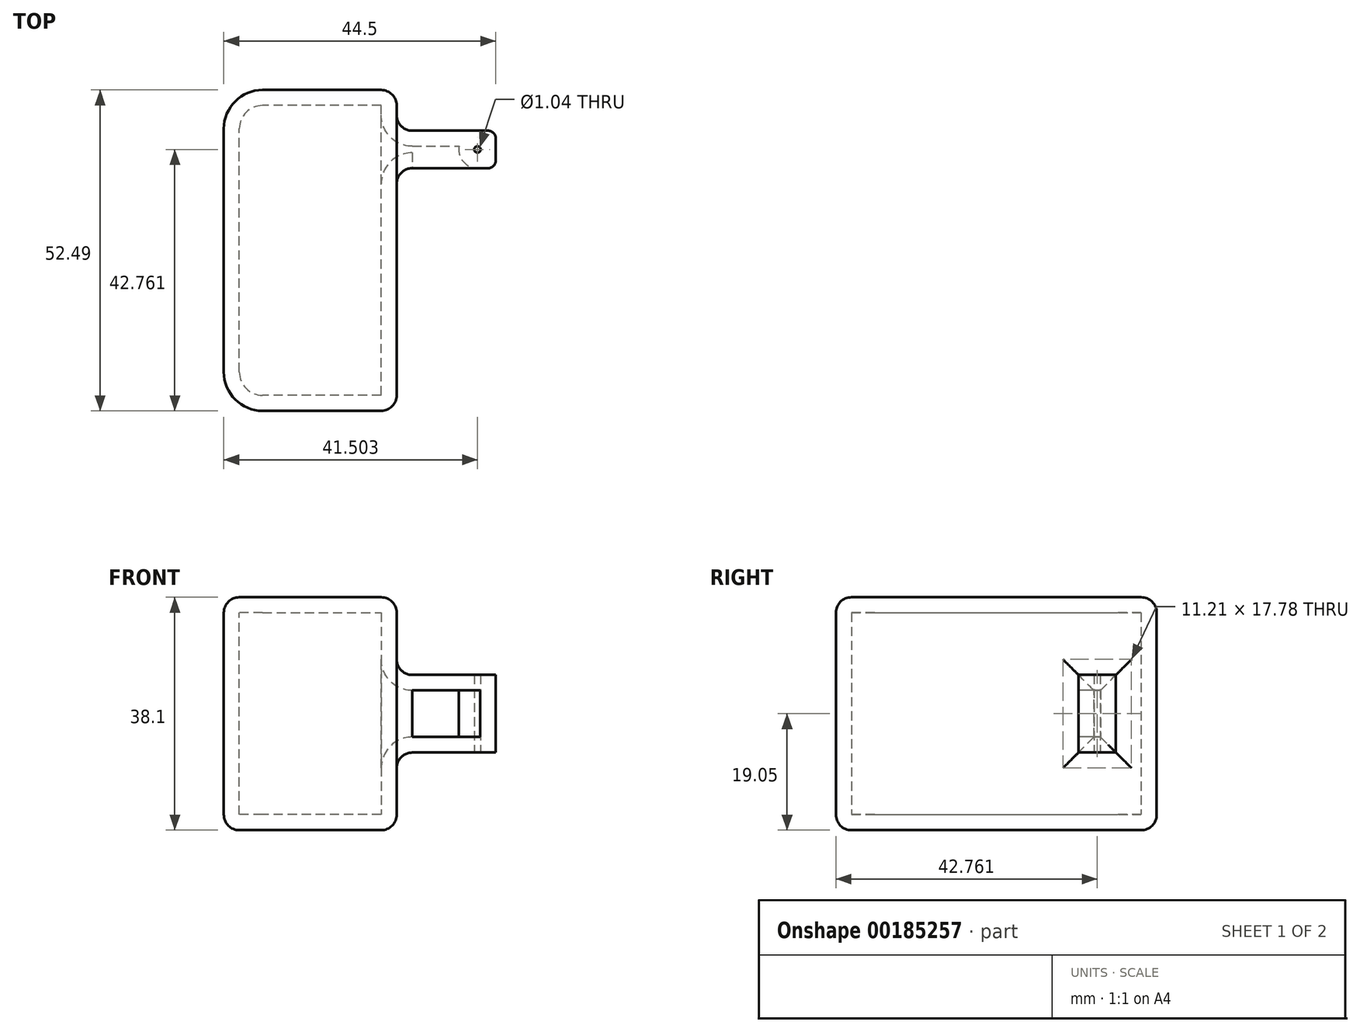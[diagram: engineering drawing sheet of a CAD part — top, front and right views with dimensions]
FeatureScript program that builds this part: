
annotation { "Feature Type Name" : "Feature", "Feature Type Description" : "" }
export const myFeature = defineFeature(function(context is Context, id is Id, definition is map)
    precondition{}
    {
        {
            var Q0;
            Q0=qCreatedBy(makeId("Top.planeOp"),FACE);
            var sketch = newSketch(context, id + "F0", { "sketchPlane" : qUnion([Q0])});
            skLineSegment(sketch, "E0.bottom", {"start": v(6.35, 0) * mm, "end": v(28.29, 0) * mm});
            skLineSegment(sketch, "E0.top", {"start": v(6.35, 52.5) * mm, "end": v(28.29, 52.5) * mm});
            skLineSegment(sketch, "E0.left", {"start": v(0, 6.35) * mm, "end": v(0, 46.14) * mm});
            skLineSegment(sketch, "E0.right", {"start": v(28.29, 0) * mm, "end": v(28.29, 52.5) * mm});
            skLineSegment(sketch, "E1.bottom", {"start": v(28.29, 45.83) * mm, "end": v(43.23, 45.83) * mm});
            skLineSegment(sketch, "E1.top", {"start": v(28.29, 39.7) * mm, "end": v(43.23, 39.7) * mm});
            skLineSegment(sketch, "E1.left", {"start": v(28.29, 45.83) * mm, "end": v(28.29, 39.7) * mm});
            skLineSegment(sketch, "E1.right", {"start": v(44.5, 44.56) * mm, "end": v(44.5, 40.97) * mm});
            skPoint(sketch, "E2.visualSharp", {"position": v(0, 52.5) * mm});
            skArc(sketch, "E2.filletArc", {"start": v(6.35, 52.5) * mm, "mid": v(1.86, 50.63) * mm, "end": v(0, 46.14) * mm});
            skPoint(sketch, "E3.visualSharp", {"position": v(0, 0) * mm});
            skArc(sketch, "E3.filletArc", {"start": v(0, 6.35) * mm, "mid": v(1.86, 1.86) * mm, "end": v(6.35, 0) * mm});
            skCircle(sketch, "E4", {"center": v(41.5, 42.76) * mm, "radius": 0.52 * mm});
            skPoint(sketch, "E5.visualSharp", {"position": v(44.5, 45.83) * mm});
            skArc(sketch, "E5.filletArc", {"start": v(44.5, 44.56) * mm, "mid": v(44.12, 45.46) * mm, "end": v(43.23, 45.83) * mm});
            skPoint(sketch, "E6.visualSharp", {"position": v(44.5, 39.7) * mm});
            skArc(sketch, "E6.filletArc", {"start": v(43.23, 39.7) * mm, "mid": v(44.12, 40.07) * mm, "end": v(44.5, 40.97) * mm});
            skPoint(sketch, "E7", {"position": v(44.5, 42.76) * mm});
            skSolve(sketch);
        }
        {
            var Q0;
            {var subQ1=sQuery(id+"F0.wireOp",EDGE,"E0.bottom");Q0=makeQuery(id+"F0.imprint","IMPRINT",FACE,{"disambiguationData":[TD([[makeQuery(id+"F0.imprint","IMPRINT",EDGE,{"derivedFrom":subQ1}),1.0]])]});}
            extrude(context, id + "F1", {"entities" : qUnion([Q0]), "endBound" : BoundingType.SYMMETRIC, "depth" : 38.1 * mm});
        }
        {
            var Q0;
            Q0=makeQuery(id+"F0.imprint","IMPRINT",FACE,{"disambiguationData":[TD([[makeQuery(id+"F0.imprint","IMPRINT",EDGE,{"derivedFrom":sQuery(id+"F0.wireOp",EDGE,"E1.bottom")}),-1.0]])]});
            extrude(context, id + "F2", {"entities" : qUnion([Q0]), "operationType" : NewBodyOperationType.ADD, "endBound" : BoundingType.SYMMETRIC, "depth" : 12.7 * mm});
        }
        {
            var Q0;
            Q0=makeQuery(id+"F1.opExtrude","SWEPT_FACE",FACE,{"disambiguationData":[OSD([sQuery(id+"F0.wireOp",EDGE,"E0.right"),sQuery(id+"F0.wireOp",EDGE,"E1.left")])]});
            var Q1;
            Q1=makeQuery(id+"F1.opExtrude","SWEPT_EDGE",EDGE,{"disambiguationData":[OSD([sQuery(id+"F0.wireOp",EDGE,"E0.top"),sQuery(id+"F0.wireOp",EDGE,"E0.right")])]});
            var Q2;
            Q2=makeQuery(id+"F1.opExtrude","CAP_EDGE",EDGE,{"disambiguationData":[OSD([sQuery(id+"F0.wireOp",EDGE,"E0.right"),sQuery(id+"F0.wireOp",EDGE,"E1.left")])],"isStart":false});
            var Q3;
            Q3=makeQuery(id+"F1.opExtrude","SWEPT_EDGE",EDGE,{"disambiguationData":[OSD([sQuery(id+"F0.wireOp",EDGE,"E0.bottom"),sQuery(id+"F0.wireOp",EDGE,"E0.right")])]});
            var Q4;
            Q4=makeQuery(id+"F1.opExtrude","CAP_EDGE",EDGE,{"disambiguationData":[OSD([sQuery(id+"F0.wireOp",EDGE,"E0.top")])],"isStart":true});
            var Q5;
            Q5=makeQuery(id+"F1.opExtrude","CAP_EDGE",EDGE,{"disambiguationData":[OSD([sQuery(id+"F0.wireOp",EDGE,"E0.top")])],"isStart":false});
            fillet(context, id + "F3", {"entities" : qUnion([Q0, Q1, Q2, Q3, Q4, Q5]), "radius" : 2.54 * mm, "tangentPropagation" : true, "allowEdgeOverflow" : false});
        }
        {
            var Q0;
            Q0=makeQuery(id+"F2.opExtrude","SWEPT_FACE",FACE,{"disambiguationData":[OSD([sQuery(id+"F0.wireOp",EDGE,"E1.top")])]});
            shell(context, id + "F4", {"entities" : qUnion([Q0]), "thickness" : 2.54 * mm});
        }
    });
